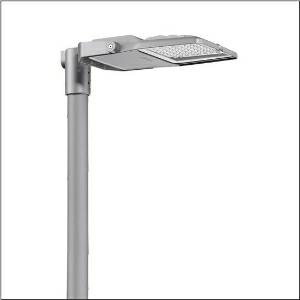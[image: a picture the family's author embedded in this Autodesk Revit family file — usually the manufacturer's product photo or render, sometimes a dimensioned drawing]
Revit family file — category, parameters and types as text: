
# Revit family: floodlight_fl_21_iq_mini___pl33t_5xa7772b2f3a_3cf2
name_source: partatom
category: Lighting Fixtures
units: mm (PartAtom-declared; Revit-internal decimal feet)

## family parameters
Cut with Voids When Loaded = No
Host = Face
Light Source = No
Part Type = Normal
Room Calculation Point = No
Round Connector Dimension = Use Diameter
Shared = No

## types (1)
- --- (1 x LED, 6170 lm, 45.5 W, 3000K)
    Apparent Load = 46 VA
    CIE Flux Codes = 26 75 99 100 100
    Color Rendering = 70
    Color Temperature = 3000K
    Default Elevation = 1800 mm
    Description = Floodlight FL 21 iQ mini, floodlight, primary light control with lens, of PMMA, primary optical cover: protective disc, of toughened safety glass, transparent, light distribution: PL33T, light emission: direct distribution, installation type: surface-mounted, lamps: LED, High Power LED, rated values: 6.170lm | 45,5W | 135,6lm/W (begin service life); end service life: 6.170lm | 48W; at 50% lumin. flux: 3.085lm | 21,5W | 143,5lm/W, colour temperature: 3000K, colour rendering: CRI > 70, light colour: 730, light setting 1 begin service life: 100% | 6.170lm | 45,5W | 135,6lm/W | 3.000K, light setting 1 end service life: 48W, further light settings possible, control: pre-setting: linear dimming characteristic, Auto-Match, Temp-Guard, Night-Set, Smart-Wire, Desk-Remote (wireless, voltage-free reading and setting of iQ features in the workshop via application-optimized NFC function/RFID function), optimised constant luminous flux control (CLO 2.0), Light-Fading, Lumen-Switch, with terminal, 6-pole, mains connection: 220..240V, AC, 50/60Hz, luminaire housing, of diecast aluminium, powder-coated, SITECO metallic grey (DB 702S), corrosivity category C5 mid according to DIN EN ISO 12944suitable for swimming poolschlorine-resistant, sealing non-destructively replaceable, please order mast flange separately, mast bracket, of steel, galvanised, powder-coated, protection rating (complete): IP66, insulation class (complete): insulation class II (safety insulation), certification: CE, ENEC, VDE, protection symbol: D, impact resistance: IK08, permissible operating ambient temperature: -40..+40°C, permissible operating ambient temperature for outdoor applications: -40..+50°C, standard: DIN EN 12944, LABS conformity tested according to VDMA 24364:2018-05, packaging unit: 1 piece

Light Distribution: PL33T
    Height = 70 mm
    Lamp = 1 x LED
    Lamp Light Flux = 6170 lm
    Lamp Power = 45.5 W
    Lamp count = 1
    Length = 485 mm
    Luminous efficacy = 136 lm/W
    Manufacturer = Siteco
    ModVariant = No
    Model = 5XA7772B2F3A
    Number of Poles = 1
    OnlyDefault = Yes
    Power Factor = 1
    Product Name = Floodlight FL 21 iQ mini | PL33T
    Product group = floodlight | pylon annexe
    ProductGroupID = 6201
    Protection Class = Protection class II
    Protection Degree = IP 66
    RLX_Detail_Level = 1
    RLX_Emergency_Light_Flux = 0 lm
    RLX_Emergency_Type = 0
    RLX_Emergency_Type_DB = No
    RlxData = <blob elided: 101309 chars, md5=29523ca2>
    Socket = socket
    Standby Power = 0 W
    System Light Flux = 6170 lm
    System Power = 46 W
    Type Comments = factory setting: luminous flux: 100 % | dim-lin: 254 | 463 mA
    Type Image = l_1007125.jpg
    URL = http://relux.com
    VarID = @adj_149527
    Voltage = 0 V
    Weight = 0.00 kg
    Width = 337 mm

## geometry (parser evidence)
native form markers: Blend x4, Sweep x12
no freeform markers — native parametric forms only
